# Revit family: ADSK_Фундамент_ЖбКолонна_1уступ
name_source: partatom
category: Фундамент несущей конструкции
revit_build: Autodesk Revit 2017 (Build: 20160720_1515(x64)
units: mm (PartAtom-declared; Revit-internal decimal feet)

## family parameters
Всегда вертикально = Да
Заглушка = Нет
Заголовок OmniClass = Foundations
Материал для поведения модели = Прочее
На основе рабочей плоскости = Нет
Номер OmniClass = 23.25.05.00
Общий = Нет
При загрузке вырезать с полостями = Нет

## types (1)
- ADSK_Фундамент_ЖбКолонна_1уступ
    Высота стакана фундамента = 1018 мм
    Глубина заделки колонны = 618 мм
    Длина = 1800 мм
    Длина основания колонны = 500 мм
    Длина стакана фундамента = 1000 мм
    Материал несущих конструкций = <По категории>
    Свес подошвы влево = 200 мм
    Свес подошвы вперед = 300 мм
    Свес подошвы вправо = 200 мм
    Свес подошвы назад = 500 мм
    Смещение длины расч = 500 мм
    Смещение ширины расч = 400 мм
    Толщина подошвы = 311 мм
    Уширение стакана колонны = 25 мм
    Ширина = 1200 мм
    Ширина основания колонны = 300 мм
    Ширина стакана фундамента = 800 мм
    Эксцентриситет по Y = 0 мм
    Эксцентриситет по Х = 0 мм
